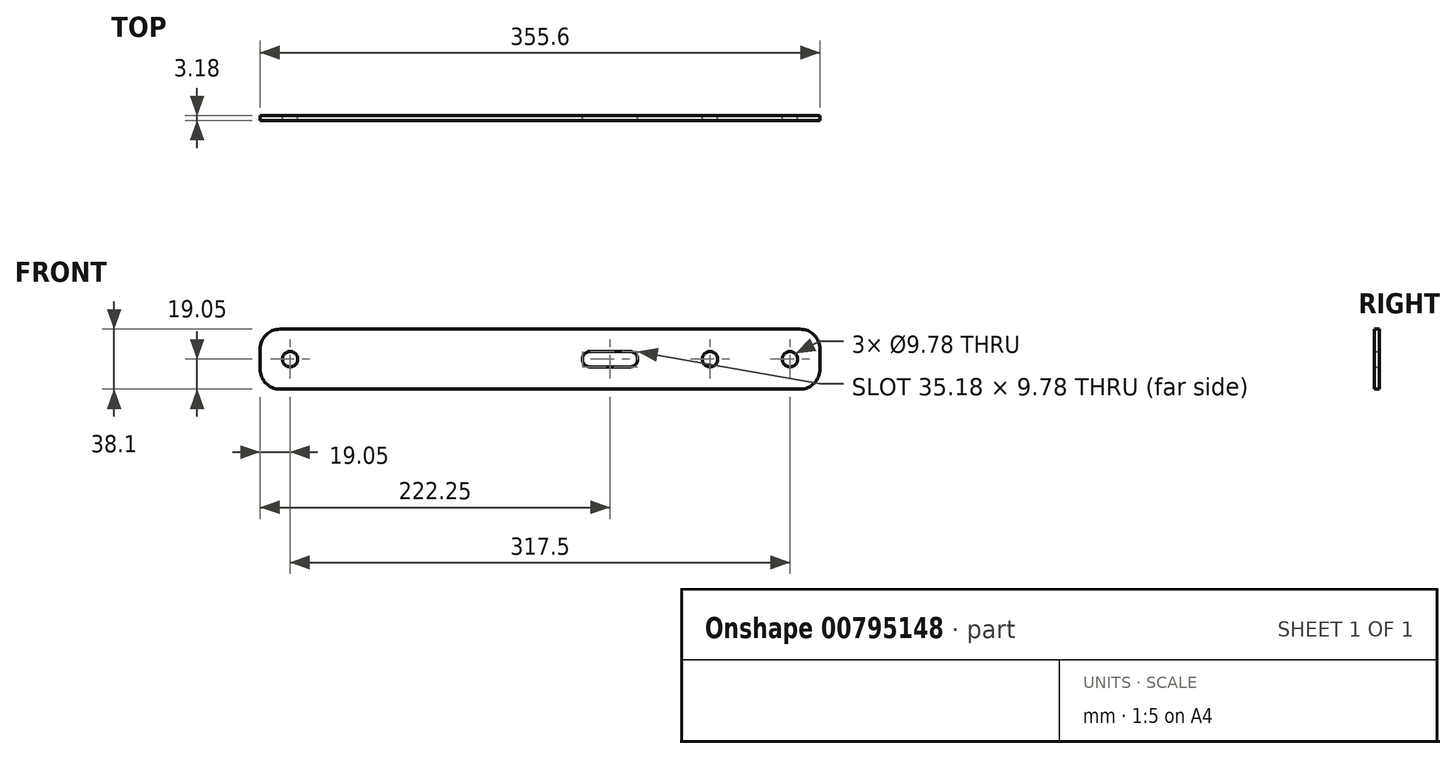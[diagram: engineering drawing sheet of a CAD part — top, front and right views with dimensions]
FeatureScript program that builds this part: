
annotation { "Feature Type Name" : "Feature", "Feature Type Description" : "" }
export const myFeature = defineFeature(function(context is Context, id is Id, definition is map)
    precondition{}
    {
        {
            var Q0;
            Q0=qCreatedBy(makeId("Front.planeOp"),FACE);
            var sketch = newSketch(context, id + "F0", { "sketchPlane" : qUnion([Q0])});
            skLineSegment(sketch, "E0.bottom", {"start": v(165.1, -19.05) * mm, "end": v(-165.1, -19.05) * mm});
            skLineSegment(sketch, "E0.top", {"start": v(165.1, 19.05) * mm, "end": v(-165.1, 19.05) * mm});
            skLineSegment(sketch, "E0.left", {"start": v(177.8, -6.35) * mm, "end": v(177.8, 6.35) * mm});
            skLineSegment(sketch, "E0.right", {"start": v(-177.8, -6.35) * mm, "end": v(-177.8, 6.35) * mm});
            skPoint(sketch, "E0.middle", {"position": v(0, 0) * mm});
            skLineSegment(sketch, "E1", {"start": v(158.75, 4.89) * mm, "end": v(158.75, 4.89) * mm});
            skCircle(sketch, "E2", {"center": v(-158.75, 0) * mm, "radius": 4.89 * mm});
            skPoint(sketch, "E2.centerSnap0", {"position": v(-177.8, 0) * mm});
            skPoint(sketch, "E3.visualSharp", {"position": v(-177.8, -19.05) * mm});
            skArc(sketch, "E3.filletArc", {"start": v(-177.8, -6.35) * mm, "mid": v(-174.08, -15.33) * mm, "end": v(-165.1, -19.05) * mm});
            skPoint(sketch, "E4.visualSharp", {"position": v(-177.8, 19.05) * mm});
            skArc(sketch, "E4.filletArc", {"start": v(-165.1, 19.05) * mm, "mid": v(-174.08, 15.33) * mm, "end": v(-177.8, 6.35) * mm});
            skPoint(sketch, "E5.visualSharp", {"position": v(177.8, -19.05) * mm});
            skArc(sketch, "E5.filletArc", {"start": v(165.1, -19.05) * mm, "mid": v(174.08, -15.33) * mm, "end": v(177.8, -6.35) * mm});
            skPoint(sketch, "E6.visualSharp", {"position": v(177.8, 19.05) * mm});
            skArc(sketch, "E6.filletArc", {"start": v(177.8, 6.35) * mm, "mid": v(174.08, 15.33) * mm, "end": v(165.1, 19.05) * mm});
            skPoint(sketch, "E7.center.orphan", {"position": v(35.83, 0) * mm});
            skPoint(sketch, "E8.start.orphan", {"position": v(35.83, -4.89) * mm});
            skPoint(sketch, "E9.center.orphan", {"position": v(17.46, 0) * mm});
            skPoint(sketch, "E9.end.orphan", {"position": v(17.46, -4.89) * mm});
            skPoint(sketch, "E10.start.orphan", {"position": v(17.46, 4.89) * mm});
            skLineSegment(sketch, "E11", {"start": v(57.15, 0) * mm, "end": v(31.75, 0) * mm});
            skPoint(sketch, "E11.startSnap0", {"position": v(71.31, 0) * mm});
            skArc(sketch, "E12.0.startCap", {"start": v(57.15, 4.89) * mm, "mid": v(62.04, 0) * mm, "end": v(57.15, -4.89) * mm});
            skArc(sketch, "E12.0.endCap", {"start": v(31.75, -4.89) * mm, "mid": v(26.86, 0) * mm, "end": v(31.75, 4.89) * mm});
            skLineSegment(sketch, "E12.0.left", {"start": v(57.15, -4.89) * mm, "end": v(31.75, -4.89) * mm});
            skLineSegment(sketch, "E12.0.right", {"start": v(57.15, 4.89) * mm, "end": v(31.75, 4.89) * mm});
            skPoint(sketch, "E13.orphan", {"position": v(107.95, -4.89) * mm});
            skPoint(sketch, "E14.center.orphan", {"position": v(107.95, 0) * mm});
            skPoint(sketch, "E15.center.orphan", {"position": v(158.75, 0) * mm});
            skPoint(sketch, "E15.start.orphan", {"position": v(158.75, -4.89) * mm});
            skCircle(sketch, "E16", {"center": v(107.95, 0) * mm, "radius": 4.89 * mm});
            skCircle(sketch, "E17", {"center": v(158.75, 0) * mm, "radius": 4.89 * mm});
            skSolve(sketch);
        }
        {
            var Q0;
            Q0=makeQuery(id+"F0.imprint","IMPRINT",FACE,{"disambiguationData":[TD([[makeQuery(id+"F0.imprint","IMPRINT",EDGE,{"derivedFrom":sQuery(id+"F0.wireOp",EDGE,"E0.bottom")}),-1.0]])]});
            extrude(context, id + "F1", {"entities" : qUnion([Q0]), "depth" : 3.17 * mm, "offsetDistance" : 25.4 * mm});
        }
    });
